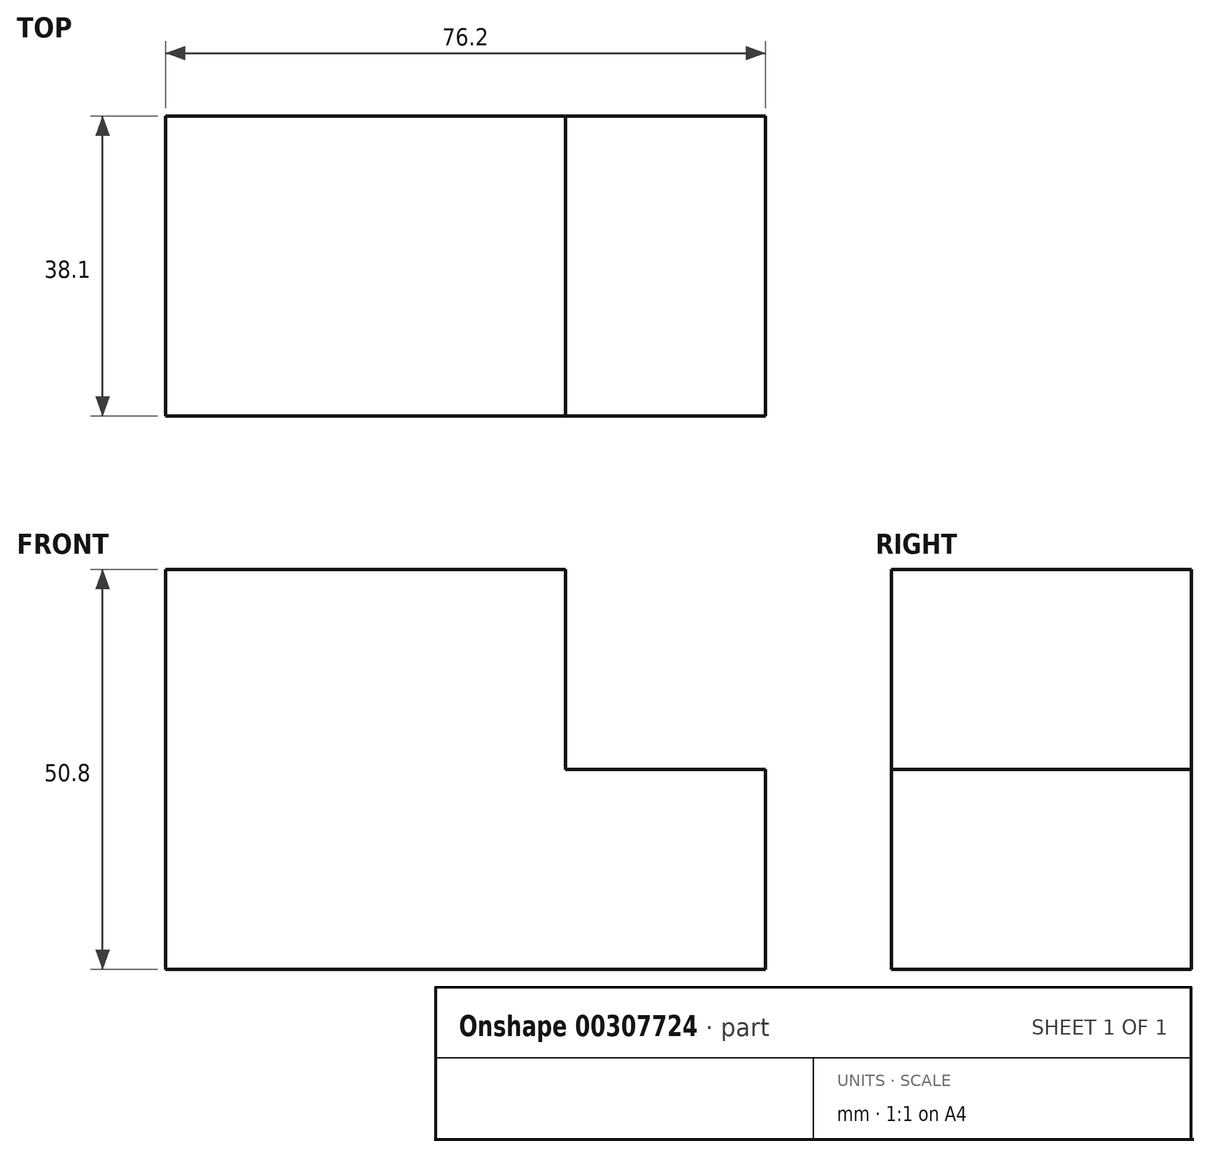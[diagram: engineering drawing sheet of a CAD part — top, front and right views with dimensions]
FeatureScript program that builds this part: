
annotation { "Feature Type Name" : "Feature", "Feature Type Description" : "" }
export const myFeature = defineFeature(function(context is Context, id is Id, definition is map)
    precondition{}
    {
        {
            var Q0;
            Q0=qCreatedBy(makeId("Front.planeOp"),FACE);
            var sketch = newSketch(context, id + "F0", { "sketchPlane" : qUnion([Q0])});
            skLineSegment(sketch, "E0", {"start": v(-35.67, -50.8) * mm, "end": v(40.53, -50.8) * mm});
            skLineSegment(sketch, "E1", {"start": v(40.53, -50.8) * mm, "end": v(40.53, -25.4) * mm});
            skLineSegment(sketch, "E2", {"start": v(40.53, -25.4) * mm, "end": v(15.13, -25.4) * mm});
            skLineSegment(sketch, "E3", {"start": v(15.13, -25.4) * mm, "end": v(15.13, 0) * mm});
            skLineSegment(sketch, "E4", {"start": v(15.13, 0) * mm, "end": v(-35.67, 0) * mm});
            skLineSegment(sketch, "E5", {"start": v(-35.67, 0) * mm, "end": v(-35.67, -50.8) * mm});
            skSolve(sketch);
        }
        {
            var Q0;
            Q0=makeQuery(id+"F0.imprint","IMPRINT",FACE,{"disambiguationData":[TD([[makeQuery(id+"F0.imprint","IMPRINT",EDGE,{"derivedFrom":sQuery(id+"F0.wireOp",EDGE,"E0")}),1.0]])]});
            extrude(context, id + "F1", {"entities" : qUnion([Q0]), "depth" : 38.1 * mm});
        }
    });
